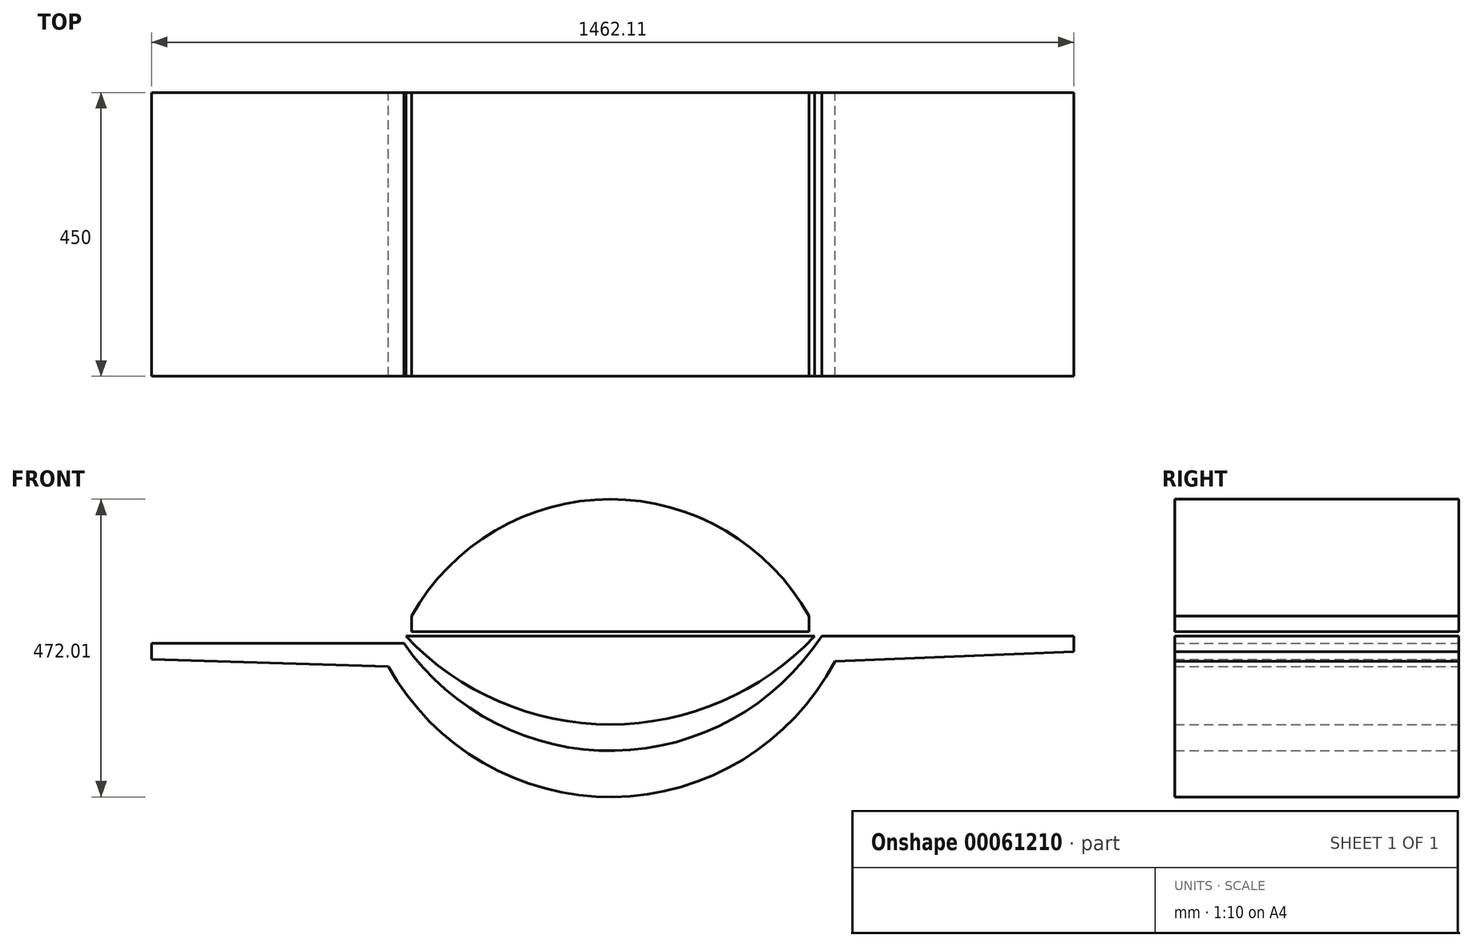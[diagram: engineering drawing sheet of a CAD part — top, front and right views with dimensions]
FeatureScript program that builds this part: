
annotation { "Feature Type Name" : "Feature", "Feature Type Description" : "" }
export const myFeature = defineFeature(function(context is Context, id is Id, definition is map)
    precondition{}
    {
        {
            var Q0;
            Q0=qCreatedBy(makeId("Front.planeOp"),FACE);
            var sketch = newSketch(context, id + "F0", { "sketchPlane" : qUnion([Q0])});
            skArc(sketch, "E0", {"start": v(315, 286.57) * mm, "mid": v(0, 472) * mm, "end": v(-315, 286.57) * mm});
            skLineSegment(sketch, "E1", {"start": v(-315, 286.57) * mm, "end": v(-315, 262) * mm});
            skLineSegment(sketch, "E2", {"start": v(-315, 262) * mm, "end": v(315, 262) * mm});
            skLineSegment(sketch, "E3", {"start": v(315, 262) * mm, "end": v(315, 286.57) * mm});
            skArc(sketch, "E4", {"start": v(-324, 254.88) * mm, "mid": v(0, 114.88) * mm, "end": v(324, 254.88) * mm});
            skLineSegment(sketch, "E5", {"start": v(-324, 254.88) * mm, "end": v(324, 254.88) * mm});
            skLineSegment(sketch, "E6", {"start": v(-727.09, 218.28) * mm, "end": v(-727.09, 243.28) * mm});
            skLineSegment(sketch, "E7", {"start": v(-727.09, 243.28) * mm, "end": v(-327.09, 243.28) * mm});
            skLineSegment(sketch, "E8", {"start": v(-727.09, 218.28) * mm, "end": v(-351.94, 206.96) * mm});
            skLineSegment(sketch, "E9", {"start": v(356.24, 214.9) * mm, "end": v(735.02, 230.02) * mm});
            skLineSegment(sketch, "E10", {"start": v(735.02, 230.02) * mm, "end": v(735.02, 255.02) * mm});
            skLineSegment(sketch, "E11", {"start": v(735.02, 255.02) * mm, "end": v(335.02, 255.02) * mm});
            skArc(sketch, "E12", {"start": v(-327.09, 243.28) * mm, "mid": v(7.08, 73.26) * mm, "end": v(335.02, 255.02) * mm});
            skArc(sketch, "E13", {"start": v(-351.94, 206.96) * mm, "mid": v(4.52, 0.03) * mm, "end": v(356.24, 214.9) * mm});
            skLineSegment(sketch, "E14", {"start": v(0, -690.86) * mm, "end": v(0, 705.33) * mm, "construction": true});
            skSolve(sketch);
        }
        {
            var Q0;
            Q0=makeQuery(id+"F0.imprint","IMPRINT",FACE,{"disambiguationData":[TD([[makeQuery(id+"F0.imprint","IMPRINT",EDGE,{"derivedFrom":sQuery(id+"F0.wireOp",EDGE,"E0")}),1.0]])]});
            extrude(context, id + "F1", {"entities" : qUnion([Q0]), "endBound" : BoundingType.SYMMETRIC, "depth" : 450 * mm});
        }
        {
            var Q0;
            Q0=makeQuery(id+"F0.imprint","IMPRINT",FACE,{"disambiguationData":[TD([[makeQuery(id+"F0.imprint","IMPRINT",EDGE,{"derivedFrom":sQuery(id+"F0.wireOp",EDGE,"E6")}),-1.0]])]});
            var Q1;
            Q1=makeQuery(id+"F0.imprint","IMPRINT",FACE,{"disambiguationData":[TD([[makeQuery(id+"F0.imprint","IMPRINT",EDGE,{"derivedFrom":sQuery(id+"F0.wireOp",EDGE,"E4")}),1.0]])]});
            extrude(context, id + "F2", {"entities" : qUnion([Q0, Q1]), "endBound" : BoundingType.SYMMETRIC, "depth" : 450 * mm});
        }
    });
